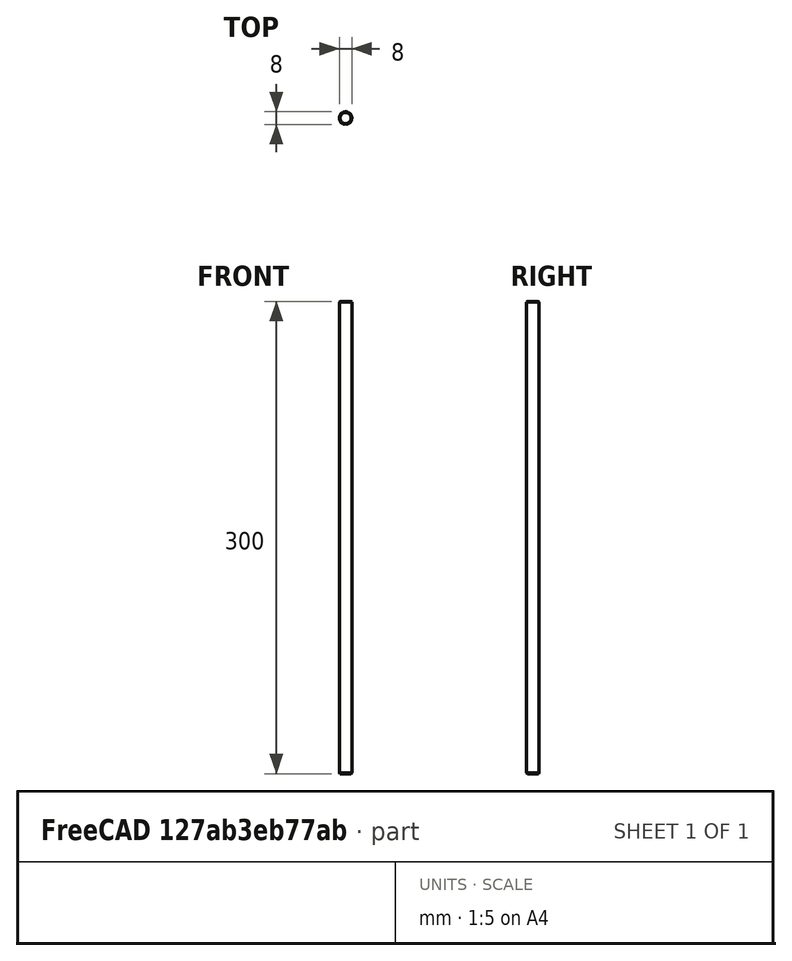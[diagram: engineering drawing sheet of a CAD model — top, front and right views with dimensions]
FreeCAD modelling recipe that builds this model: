
FCSTD DOCUMENT  (FreeCAD 0.21R33771 (Git))
Label: 300mm rod
License: All rights reserved
LicenseURL: http://en.wikipedia.org/wiki/All_rights_reserved
objects: Sketcher::SketchObject×1, PartDesign::Pad×1, PartDesign::Chamfer×1, PartDesign::Body×1
note: 6 computed .brp shape members not serialized (recipe doc carries the construction recipe); baked Part::Feature solids carry a one-line shape summary decoded from their .brp

FEATURE [Sketcher::SketchObject] Sketch
  FullyConstrained = true
  MapMode = 5
  Support = -> [XY_Plane]
  sketch-geometry (1):
    g0: Circle CenterX=0 CenterY=0 CenterZ=0 NormalX=0 NormalY=0 NormalZ=1 AngleXU=0 Radius=4
  constraints (2):
    c: Coincident(g0,g-1)
    c: Diameter(g0) = 8
FEATURE [PartDesign::Pad] Pad
  Direction = (0,0,1)
  Length = 300
  Length2 = 10
  Profile = -> Sketch
  ReferenceAxis = -> Sketch [N_Axis]
  Type = 0
FEATURE [PartDesign::Chamfer] Chamfer
  Angle = 45
  Base = -> Pad [Edge2,Edge3]
  BaseFeature = -> Pad
  ChamferType = 0
  FlipDirection = false
  Size = 0.5
  Size2 = 1
  SupportTransform = false
  UseAllEdges = false
FEATURE [PartDesign::Body] Body
  Group = -> [Sketch,Pad,Chamfer]
  Origin = -> Origin
  Tip = -> Chamfer
